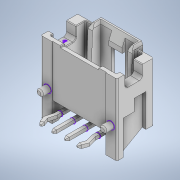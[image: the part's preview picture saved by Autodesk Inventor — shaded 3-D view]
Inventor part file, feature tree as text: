
AUTODESK INVENTOR PART (.ipt)
format: ipt  version: 2022 (Build 260153000, 153)  size: 347,648 bytes
history: native  units: in
note: dims shown in document units (in); Inventor stores cm internally (conversion verified against a paired STEP export)
features: sketch x2, other x1, extrude x1, imported_body x1
ambient origin geometry x8: Origin, YZ Plane, XZ Plane, XY Plane, X Axis, Y Axis, Z Axis, Center Point
bodies: Solid1 (feature_tree)
feature tree (5):
  other  "Repaired Geometry1"
  extrude  "Extrusion1"  [1 undecoded]
  sketch  "3D Sketch1"
  sketch  "Sketch1"  dims[d0=0.0039in d1=0.0in]
  imported_body  "Base1"
note: 1 required parameter value undecoded (feature->parameter linkage not recoverable at this tier; creation-order binding heuristic only, values carry confidence <= 0.55)
